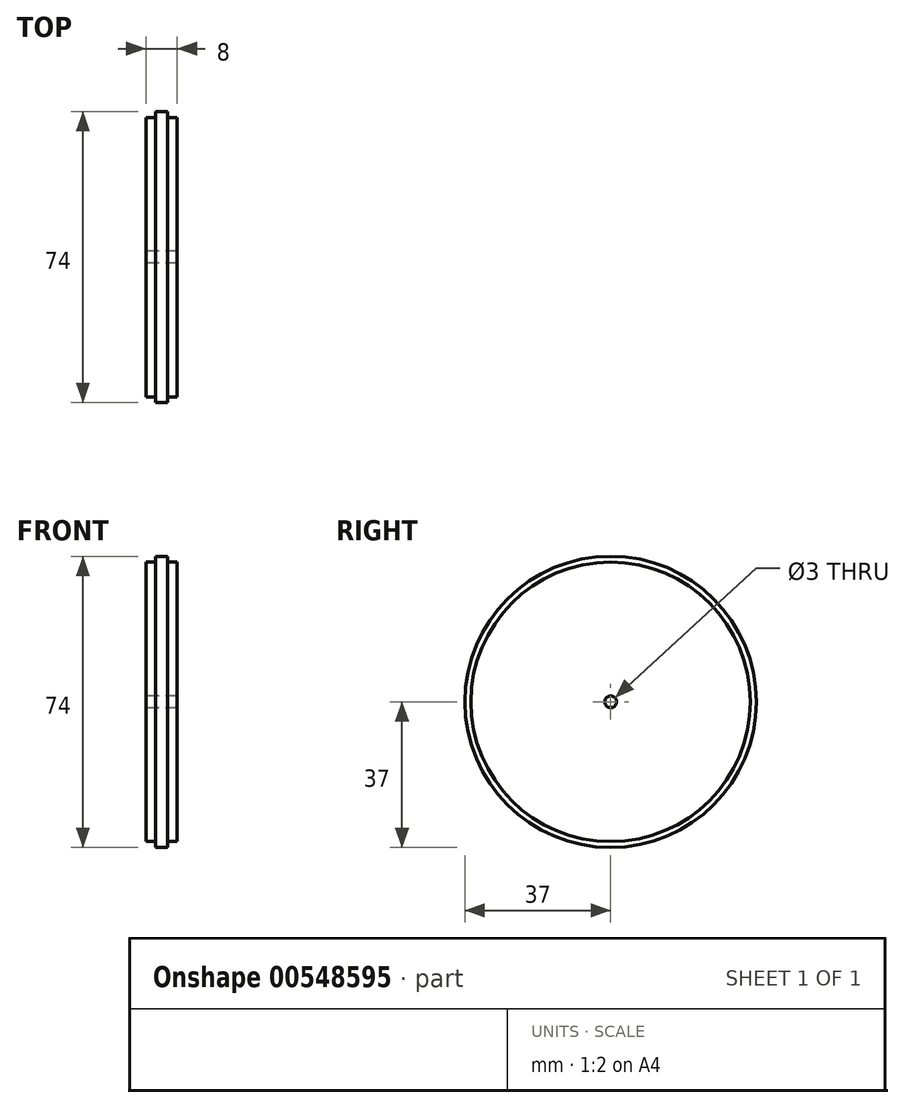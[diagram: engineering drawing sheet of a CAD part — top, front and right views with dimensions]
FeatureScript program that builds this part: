
annotation { "Feature Type Name" : "Feature", "Feature Type Description" : "" }
export const myFeature = defineFeature(function(context is Context, id is Id, definition is map)
    precondition{}
    {
        {
            var Q0;
            Q0=qCreatedBy(makeId("Right.planeOp"),FACE);
            var sketch = newSketch(context, id + "F0", { "sketchPlane" : qUnion([Q0])});
            skCircle(sketch, "E0", {"center": v(0, 0) * mm, "radius": 35.5 * mm});
            skCircle(sketch, "E1", {"center": v(0, 0) * mm, "radius": 37 * mm});
            skCircle(sketch, "E2", {"center": v(0, 0) * mm, "radius": 1.5 * mm});
            skSolve(sketch);
        }
        {
            var Q0;
            Q0=makeQuery(id+"F0.imprint","IMPRINT",FACE,{"disambiguationData":[TD([[makeQuery(id+"F0.imprint","IMPRINT",EDGE,{"derivedFrom":sQuery(id+"F0.wireOp",EDGE,"E0")}),-1.0]])]});
            extrude(context, id + "F1", {"entities" : qUnion([Q0]), "endBound" : BoundingType.SYMMETRIC, "depth" : 3 * mm, "offsetDistance" : 25 * mm});
        }
        {
            var Q0;
            Q0=makeQuery(id+"F0.imprint","IMPRINT",FACE,{"disambiguationData":[TD([[makeQuery(id+"F0.imprint","IMPRINT",EDGE,{"derivedFrom":sQuery(id+"F0.wireOp",EDGE,"E0")}),1.0]])]});
            extrude(context, id + "F2", {"entities" : qUnion([Q0]), "operationType" : NewBodyOperationType.ADD, "endBound" : BoundingType.SYMMETRIC, "depth" : 8 * mm, "offsetDistance" : 25 * mm});
        }
    });
